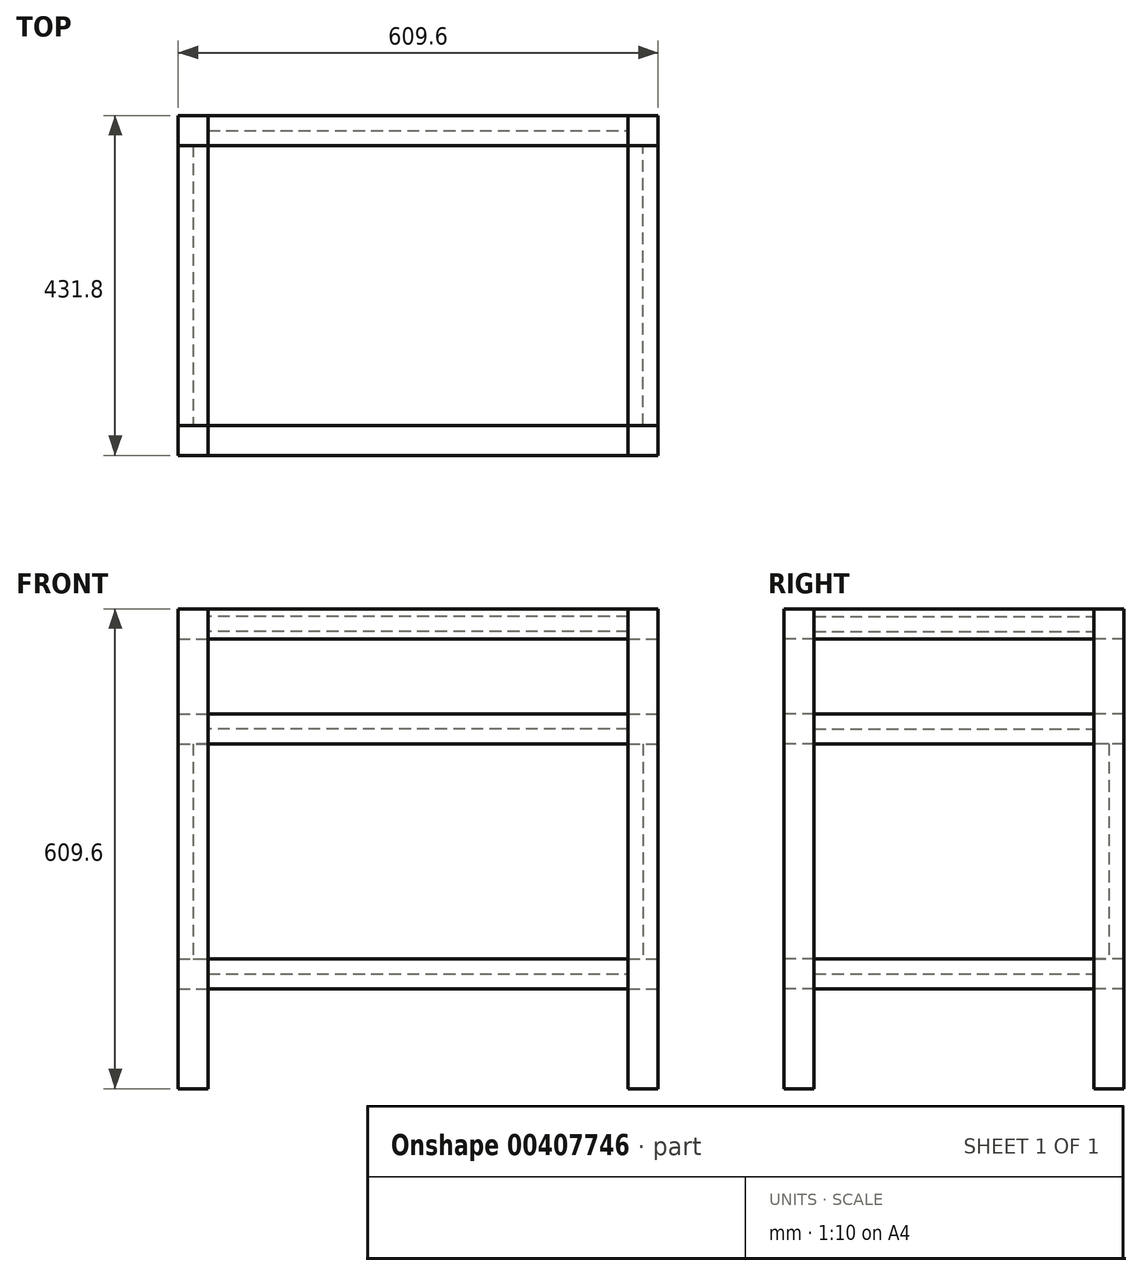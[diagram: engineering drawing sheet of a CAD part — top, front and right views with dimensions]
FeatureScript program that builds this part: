
annotation { "Feature Type Name" : "Feature", "Feature Type Description" : "" }
export const myFeature = defineFeature(function(context is Context, id is Id, definition is map)
    precondition{}
    {
        {
            var Q0;
            Q0=qCreatedBy(makeId("Top.planeOp"),FACE);
            var sketch = newSketch(context, id + "F0", { "sketchPlane" : qUnion([Q0])});
            skLineSegment(sketch, "E0.bottom", {"start": v(-304.8, 215.9) * mm, "end": v(304.8, 215.9) * mm, "construction": true});
            skLineSegment(sketch, "E0.top", {"start": v(-304.8, -215.9) * mm, "end": v(304.8, -215.9) * mm, "construction": true});
            skLineSegment(sketch, "E0.left", {"start": v(-304.8, 215.9) * mm, "end": v(-304.8, -215.9) * mm, "construction": true});
            skLineSegment(sketch, "E0.right", {"start": v(304.8, 215.9) * mm, "end": v(304.8, -215.9) * mm, "construction": true});
            skPoint(sketch, "E0.middle", {"position": v(0, 0) * mm});
            skLineSegment(sketch, "E1.bottom", {"start": v(-304.8, -215.9) * mm, "end": v(-266.7, -215.9) * mm});
            skLineSegment(sketch, "E1.top", {"start": v(-304.8, -177.8) * mm, "end": v(-266.7, -177.8) * mm});
            skLineSegment(sketch, "E1.left", {"start": v(-304.8, -215.9) * mm, "end": v(-304.8, -177.8) * mm});
            skLineSegment(sketch, "E1.right", {"start": v(-266.7, -215.9) * mm, "end": v(-266.7, -177.8) * mm});
            skLineSegment(sketch, "E2.MirrorCS", {"start": v(-266.7, 215.9) * mm, "end": v(-266.7, 177.8) * mm});
            skLineSegment(sketch, "E3.MirrorCS", {"start": v(-304.8, 177.8) * mm, "end": v(-266.7, 177.8) * mm});
            skLineSegment(sketch, "E4.MirrorCS", {"start": v(-304.8, 215.9) * mm, "end": v(-304.8, 177.8) * mm});
            skLineSegment(sketch, "E5.MirrorCS", {"start": v(-304.8, 215.9) * mm, "end": v(-266.7, 215.9) * mm});
            skLineSegment(sketch, "E6.MirrorCS", {"start": v(266.7, -215.9) * mm, "end": v(266.7, -177.8) * mm});
            skLineSegment(sketch, "E7.MirrorCS", {"start": v(304.8, -177.8) * mm, "end": v(266.7, -177.8) * mm});
            skLineSegment(sketch, "E8.MirrorCS", {"start": v(304.8, -215.9) * mm, "end": v(304.8, -177.8) * mm});
            skLineSegment(sketch, "E9.MirrorCS", {"start": v(304.8, -215.9) * mm, "end": v(266.7, -215.9) * mm});
            skLineSegment(sketch, "E10.MirrorCS", {"start": v(304.8, 177.8) * mm, "end": v(266.7, 177.8) * mm});
            skLineSegment(sketch, "E11.MirrorCS", {"start": v(304.8, 215.9) * mm, "end": v(304.8, 177.8) * mm});
            skLineSegment(sketch, "E12.MirrorCS", {"start": v(304.8, 215.9) * mm, "end": v(266.7, 215.9) * mm});
            skLineSegment(sketch, "E13.MirrorCS", {"start": v(266.7, 215.9) * mm, "end": v(266.7, 177.8) * mm});
            skSolve(sketch);
        }
        {
            var Q0;
            Q0=makeQuery(id+"F0.imprint","IMPRINT",FACE,{"disambiguationData":[TD([[makeQuery(id+"F0.imprint","IMPRINT",EDGE,{"derivedFrom":sQuery(id+"F0.wireOp",EDGE,"E1.bottom")}),1.0]])]});
            var Q1;
            Q1=makeQuery(id+"F0.imprint","IMPRINT",FACE,{"disambiguationData":[TD([[makeQuery(id+"F0.imprint","IMPRINT",EDGE,{"derivedFrom":sQuery(id+"F0.wireOp",EDGE,"E2.MirrorCS")}),-1.0]])]});
            var Q2;
            Q2=makeQuery(id+"F0.imprint","IMPRINT",FACE,{"disambiguationData":[TD([[makeQuery(id+"F0.imprint","IMPRINT",EDGE,{"derivedFrom":sQuery(id+"F0.wireOp",EDGE,"E10.MirrorCS")}),-1.0]])]});
            var Q3;
            Q3=makeQuery(id+"F0.imprint","IMPRINT",FACE,{"disambiguationData":[TD([[makeQuery(id+"F0.imprint","IMPRINT",EDGE,{"derivedFrom":sQuery(id+"F0.wireOp",EDGE,"E6.MirrorCS")}),-1.0]])]});
            extrude(context, id + "F1", {"entities" : qUnion([Q0, Q1, Q2, Q3]), "depth" : 609.6 * mm});
        }
        {
            var Q0;
            Q0=makeQuery(id+"F1.opExtrude","SWEPT_FACE",FACE,{"disambiguationData":[OSD([sQuery(id+"F0.wireOp",EDGE,"E1.right")])]});
            var sketch = newSketch(context, id + "F2", { "sketchPlane" : qUnion([Q0])});
            skLineSegment(sketch, "E14.bottom", {"start": v(-215.9, 127) * mm, "end": v(-177.8, 127) * mm});
            skLineSegment(sketch, "E14.top", {"start": v(-215.9, 165.1) * mm, "end": v(-177.8, 165.1) * mm});
            skLineSegment(sketch, "E14.left", {"start": v(-215.9, 127) * mm, "end": v(-215.9, 165.1) * mm});
            skLineSegment(sketch, "E14.right", {"start": v(-177.8, 127) * mm, "end": v(-177.8, 165.1) * mm});
            skLineSegment(sketch, "E15.MirrorCS", {"start": v(215.9, 165.1) * mm, "end": v(177.8, 165.1) * mm});
            skLineSegment(sketch, "E16.MirrorCS", {"start": v(177.8, 127) * mm, "end": v(177.8, 165.1) * mm});
            skLineSegment(sketch, "E17.MirrorCS", {"start": v(215.9, 127) * mm, "end": v(177.8, 127) * mm});
            skLineSegment(sketch, "E18.MirrorCS", {"start": v(215.9, 127) * mm, "end": v(215.9, 165.1) * mm});
            skLineSegment(sketch, "E19.bottom", {"start": v(-215.9, 609.6) * mm, "end": v(-177.8, 609.6) * mm});
            skLineSegment(sketch, "E19.top", {"start": v(-215.9, 571.5) * mm, "end": v(-177.8, 571.5) * mm});
            skLineSegment(sketch, "E19.left", {"start": v(-215.9, 609.6) * mm, "end": v(-215.9, 571.5) * mm});
            skLineSegment(sketch, "E19.right", {"start": v(-177.8, 609.6) * mm, "end": v(-177.8, 571.5) * mm});
            skLineSegment(sketch, "E20.bottom", {"start": v(-215.9, 476.25) * mm, "end": v(-177.8, 476.25) * mm});
            skLineSegment(sketch, "E20.top", {"start": v(-215.9, 438.15) * mm, "end": v(-177.8, 438.15) * mm});
            skLineSegment(sketch, "E20.left", {"start": v(-215.9, 476.25) * mm, "end": v(-215.9, 438.15) * mm});
            skLineSegment(sketch, "E20.right", {"start": v(-177.8, 476.25) * mm, "end": v(-177.8, 438.15) * mm});
            skLineSegment(sketch, "E21.MirrorCS", {"start": v(215.9, 438.15) * mm, "end": v(177.8, 438.15) * mm});
            skLineSegment(sketch, "E22.MirrorCS", {"start": v(177.8, 476.25) * mm, "end": v(177.8, 438.15) * mm});
            skLineSegment(sketch, "E23.MirrorCS", {"start": v(215.9, 476.25) * mm, "end": v(177.8, 476.25) * mm});
            skLineSegment(sketch, "E24.MirrorCS", {"start": v(215.9, 476.25) * mm, "end": v(215.9, 438.15) * mm});
            skLineSegment(sketch, "E25.MirrorCS", {"start": v(215.9, 571.5) * mm, "end": v(177.8, 571.5) * mm});
            skLineSegment(sketch, "E26.MirrorCS", {"start": v(177.8, 609.6) * mm, "end": v(177.8, 571.5) * mm});
            skLineSegment(sketch, "E27.MirrorCS", {"start": v(215.9, 609.6) * mm, "end": v(177.8, 609.6) * mm});
            skLineSegment(sketch, "E28.MirrorCS", {"start": v(215.9, 609.6) * mm, "end": v(215.9, 571.5) * mm});
            skSolve(sketch);
        }
        {
            var Q0;
            Q0 = qSketchRegion(id + "F2", true);
            extrude(context, id + "F3", {"entities" : qUnion([Q0]), "endBound" : BoundingType.UP_TO_NEXT, "depth" : 25.4 * mm});
        }
        {
            var Q0;
            Q0=makeQuery(id+"F1.opExtrude","SWEPT_FACE",FACE,{"disambiguationData":[OSD([sQuery(id+"F0.wireOp",EDGE,"E7.MirrorCS")])]});
            var sketch = newSketch(context, id + "F4", { "sketchPlane" : qUnion([Q0])});
            skLineSegment(sketch, "E29.bottom", {"start": v(-304.8, 609.6) * mm, "end": v(-266.7, 609.6) * mm});
            skLineSegment(sketch, "E29.top", {"start": v(-304.8, 571.5) * mm, "end": v(-266.7, 571.5) * mm});
            skLineSegment(sketch, "E29.left", {"start": v(-304.8, 609.6) * mm, "end": v(-304.8, 571.5) * mm});
            skLineSegment(sketch, "E29.right", {"start": v(-266.7, 609.6) * mm, "end": v(-266.7, 571.5) * mm});
            skLineSegment(sketch, "E30.bottom", {"start": v(-304.8, 476.25) * mm, "end": v(-266.7, 476.25) * mm});
            skLineSegment(sketch, "E30.top", {"start": v(-304.8, 438.15) * mm, "end": v(-266.7, 438.15) * mm});
            skLineSegment(sketch, "E30.left", {"start": v(-304.8, 476.25) * mm, "end": v(-304.8, 438.15) * mm});
            skLineSegment(sketch, "E30.right", {"start": v(-266.7, 476.25) * mm, "end": v(-266.7, 438.15) * mm});
            skLineSegment(sketch, "E31.bottom", {"start": v(-304.8, 165.1) * mm, "end": v(-266.7, 165.1) * mm});
            skLineSegment(sketch, "E31.top", {"start": v(-304.8, 127) * mm, "end": v(-266.7, 127) * mm});
            skLineSegment(sketch, "E31.left", {"start": v(-304.8, 165.1) * mm, "end": v(-304.8, 127) * mm});
            skLineSegment(sketch, "E31.right", {"start": v(-266.7, 165.1) * mm, "end": v(-266.7, 127) * mm});
            skLineSegment(sketch, "E32.MirrorCS", {"start": v(304.8, 127) * mm, "end": v(266.7, 127) * mm});
            skLineSegment(sketch, "E33.MirrorCS", {"start": v(266.7, 165.1) * mm, "end": v(266.7, 127) * mm});
            skLineSegment(sketch, "E34.MirrorCS", {"start": v(304.8, 165.1) * mm, "end": v(266.7, 165.1) * mm});
            skLineSegment(sketch, "E35.MirrorCS", {"start": v(304.8, 165.1) * mm, "end": v(304.8, 127) * mm});
            skLineSegment(sketch, "E36.MirrorCS", {"start": v(304.8, 438.15) * mm, "end": v(266.7, 438.15) * mm});
            skLineSegment(sketch, "E37.MirrorCS", {"start": v(266.7, 476.25) * mm, "end": v(266.7, 438.15) * mm});
            skLineSegment(sketch, "E38.MirrorCS", {"start": v(304.8, 476.25) * mm, "end": v(266.7, 476.25) * mm});
            skLineSegment(sketch, "E39.MirrorCS", {"start": v(304.8, 476.25) * mm, "end": v(304.8, 438.15) * mm});
            skLineSegment(sketch, "E40.MirrorCS", {"start": v(304.8, 571.5) * mm, "end": v(266.7, 571.5) * mm});
            skLineSegment(sketch, "E41.MirrorCS", {"start": v(304.8, 609.6) * mm, "end": v(304.8, 571.5) * mm});
            skLineSegment(sketch, "E42.MirrorCS", {"start": v(304.8, 609.6) * mm, "end": v(266.7, 609.6) * mm});
            skLineSegment(sketch, "E43.MirrorCS", {"start": v(266.7, 609.6) * mm, "end": v(266.7, 571.5) * mm});
            skSolve(sketch);
        }
        {
            var Q0;
            Q0 = qSketchRegion(id + "F4", true);
            extrude(context, id + "F5", {"entities" : qUnion([Q0]), "endBound" : BoundingType.UP_TO_NEXT, "depth" : 25.4 * mm});
        }
        {
            var Q0;
            Q0=makeQuery(id+"F5.opExtrude","SWEPT_FACE",FACE,{"disambiguationData":[OSD([sQuery(id+"F4.wireOp",EDGE,"E31.right")])]});
            var sketch = newSketch(context, id + "F6", { "sketchPlane" : qUnion([Q0])});
            skLineSegment(sketch, "E44.bottom", {"start": v(177.8, 165.1) * mm, "end": v(-177.8, 165.1) * mm});
            skLineSegment(sketch, "E44.top", {"start": v(177.8, 146.05) * mm, "end": v(-177.8, 146.05) * mm});
            skLineSegment(sketch, "E44.left", {"start": v(177.8, 165.1) * mm, "end": v(177.8, 146.05) * mm});
            skLineSegment(sketch, "E44.right", {"start": v(-177.8, 165.1) * mm, "end": v(-177.8, 146.05) * mm});
            skSolve(sketch);
        }
        {
            var Q0;
            Q0 = qSketchRegion(id + "F6", true);
            extrude(context, id + "F7", {"entities" : qUnion([Q0]), "endBound" : BoundingType.UP_TO_NEXT, "depth" : 25.4 * mm});
        }
        {
            var Q0;
            Q0=makeQuery(id+"F5.opExtrude","SWEPT_FACE",FACE,{"disambiguationData":[OSD([sQuery(id+"F4.wireOp",EDGE,"E34.MirrorCS")])]});
            var sketch = newSketch(context, id + "F8", { "sketchPlane" : qUnion([Q0])});
            skLineSegment(sketch, "E45.bottom", {"start": v(-266.7, -177.8) * mm, "end": v(-285.75, -177.8) * mm});
            skLineSegment(sketch, "E45.top", {"start": v(-266.7, 177.8) * mm, "end": v(-285.75, 177.8) * mm});
            skLineSegment(sketch, "E45.left", {"start": v(-266.7, -177.8) * mm, "end": v(-266.7, 177.8) * mm});
            skLineSegment(sketch, "E45.right", {"start": v(-285.75, -177.8) * mm, "end": v(-285.75, 177.8) * mm});
            skLineSegment(sketch, "E46.MirrorCS", {"start": v(285.75, -177.8) * mm, "end": v(285.75, 177.8) * mm});
            skLineSegment(sketch, "E47.MirrorCS", {"start": v(266.7, -177.8) * mm, "end": v(266.7, 177.8) * mm});
            skLineSegment(sketch, "E48.MirrorCS", {"start": v(266.7, 177.8) * mm, "end": v(285.75, 177.8) * mm});
            skLineSegment(sketch, "E49.MirrorCS", {"start": v(266.7, -177.8) * mm, "end": v(285.75, -177.8) * mm});
            skLineSegment(sketch, "E50.bottom", {"start": v(266.7, -177.8) * mm, "end": v(-266.7, -177.8) * mm, "construction": true});
            skLineSegment(sketch, "E50.top", {"start": v(266.7, -196.85) * mm, "end": v(-266.7, -196.85) * mm, "construction": true});
            skLineSegment(sketch, "E50.left", {"start": v(266.7, -177.8) * mm, "end": v(266.7, -196.85) * mm, "construction": true});
            skLineSegment(sketch, "E50.right", {"start": v(-266.7, -177.8) * mm, "end": v(-266.7, -196.85) * mm, "construction": true});
            skLineSegment(sketch, "E51.MirrorCS", {"start": v(266.7, 177.8) * mm, "end": v(266.7, 196.85) * mm});
            skLineSegment(sketch, "E52.MirrorCS", {"start": v(-266.7, 177.8) * mm, "end": v(-266.7, 196.85) * mm});
            skLineSegment(sketch, "E53.MirrorCS", {"start": v(266.7, 196.85) * mm, "end": v(-266.7, 196.85) * mm});
            skLineSegment(sketch, "E54.MirrorCS", {"start": v(266.7, 177.8) * mm, "end": v(-266.7, 177.8) * mm});
            skSolve(sketch);
        }
        {
            var Q0;
            Q0 = qSketchRegion(id + "F8", true);
            extrude(context, id + "F9", {"entities" : qUnion([Q0]), "endBound" : BoundingType.UP_TO_NEXT, "depth" : 25.4 * mm});
        }
        {
            var Q0;
            Q0=makeQuery(id+"F5.opExtrude","SWEPT_FACE",FACE,{"disambiguationData":[OSD([sQuery(id+"F4.wireOp",EDGE,"E37.MirrorCS")])]});
            var sketch = newSketch(context, id + "F10", { "sketchPlane" : qUnion([Q0])});
            skLineSegment(sketch, "E55.bottom", {"start": v(177.8, 476.25) * mm, "end": v(-177.8, 476.25) * mm});
            skLineSegment(sketch, "E55.top", {"start": v(177.8, 457.2) * mm, "end": v(-177.8, 457.2) * mm});
            skLineSegment(sketch, "E55.left", {"start": v(177.8, 476.25) * mm, "end": v(177.8, 457.2) * mm});
            skLineSegment(sketch, "E55.right", {"start": v(-177.8, 476.25) * mm, "end": v(-177.8, 457.2) * mm});
            skSolve(sketch);
        }
        {
            var Q0;
            Q0=makeQuery(id+"F10.imprint","IMPRINT",FACE,{"disambiguationData":[TD([[makeQuery(id+"F10.imprint","IMPRINT",EDGE,{"derivedFrom":sQuery(id+"F10.wireOp",EDGE,"E55.bottom")}),1.0]])]});
            extrude(context, id + "F11", {"entities" : qUnion([Q0]), "endBound" : BoundingType.UP_TO_NEXT, "depth" : 25.4 * mm});
        }
        {
            var Q0;
            Q0=makeQuery(id+"F5.opExtrude","SWEPT_FACE",FACE,{"disambiguationData":[OSD([sQuery(id+"F4.wireOp",EDGE,"E43.MirrorCS")])]});
            var sketch = newSketch(context, id + "F12", { "sketchPlane" : qUnion([Q0])});
            skLineSegment(sketch, "E56.bottom", {"start": v(177.8, 600.08) * mm, "end": v(-177.8, 600.08) * mm});
            skLineSegment(sketch, "E56.top", {"start": v(177.8, 581.03) * mm, "end": v(-177.8, 581.03) * mm});
            skLineSegment(sketch, "E56.left", {"start": v(177.8, 600.08) * mm, "end": v(177.8, 581.03) * mm});
            skLineSegment(sketch, "E56.right", {"start": v(-177.8, 600.08) * mm, "end": v(-177.8, 581.03) * mm});
            skSolve(sketch);
        }
        {
            var Q0;
            Q0 = qSketchRegion(id + "F12", true);
            extrude(context, id + "F13", {"entities" : qUnion([Q0]), "endBound" : BoundingType.UP_TO_NEXT, "depth" : 25.4 * mm});
        }
    });
